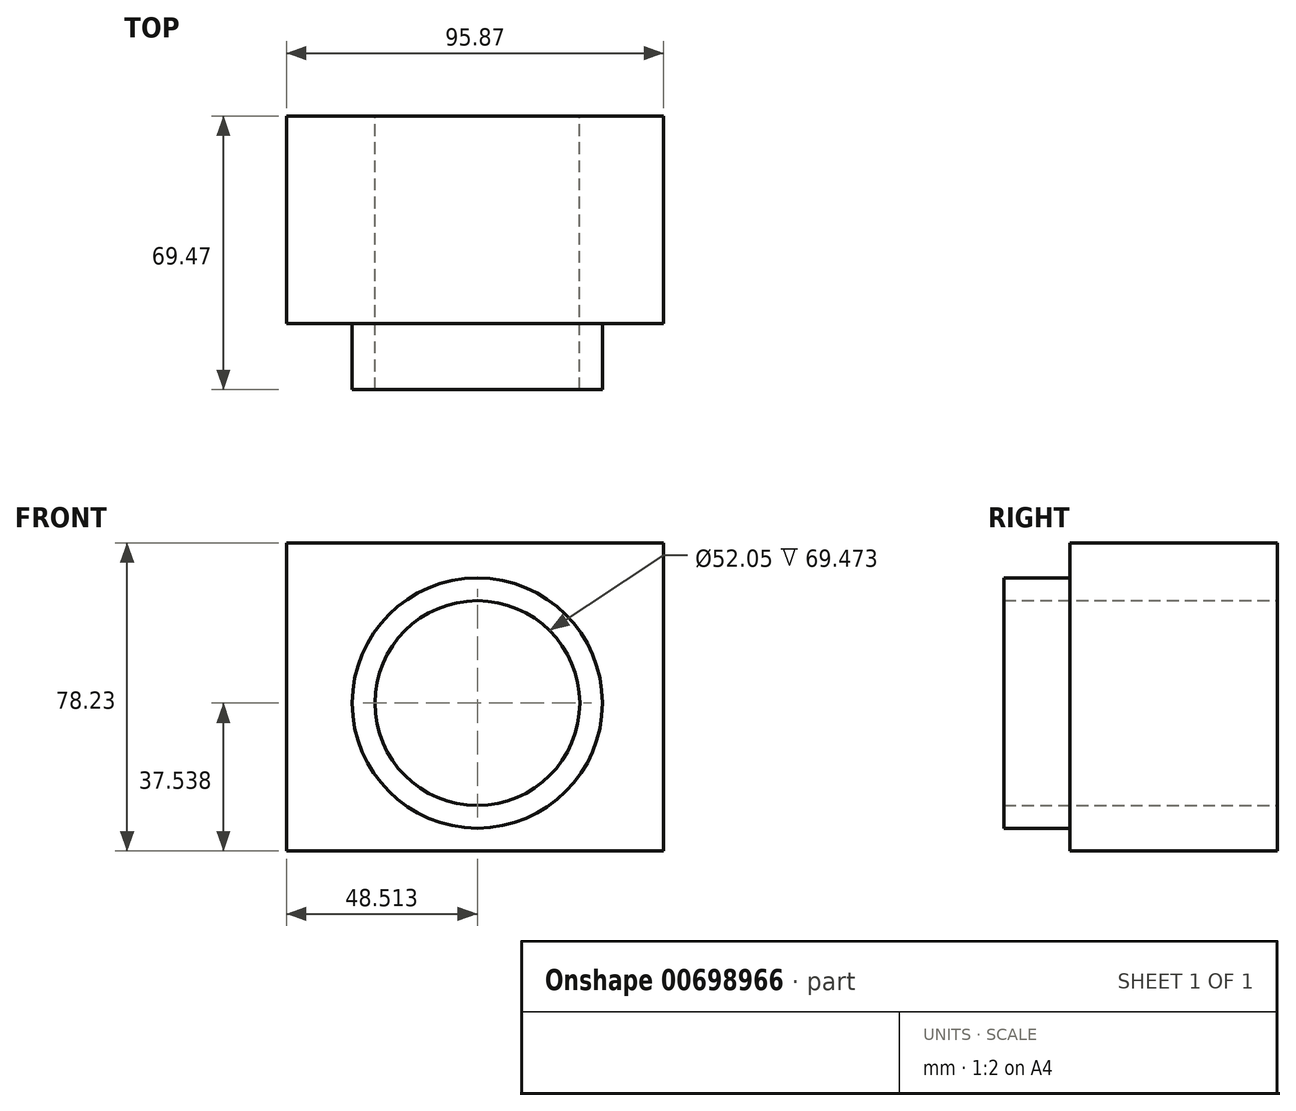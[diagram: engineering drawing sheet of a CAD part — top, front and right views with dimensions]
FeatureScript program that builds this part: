
annotation { "Feature Type Name" : "Feature", "Feature Type Description" : "" }
export const myFeature = defineFeature(function(context is Context, id is Id, definition is map)
    precondition{}
    {
        {
            var Q0;
            Q0=qCreatedBy(makeId("Top.planeOp"),FACE);
            var sketch = newSketch(context, id + "F0", { "sketchPlane" : qUnion([Q0])});
            skLineSegment(sketch, "E0.bottom", {"start": v(-36.09, -29.74) * mm, "end": v(59.78, -29.74) * mm});
            skLineSegment(sketch, "E0.top", {"start": v(-36.09, 22.97) * mm, "end": v(59.78, 22.97) * mm});
            skLineSegment(sketch, "E0.left", {"start": v(-36.09, -29.74) * mm, "end": v(-36.09, 22.97) * mm});
            skLineSegment(sketch, "E0.right", {"start": v(59.78, -29.74) * mm, "end": v(59.78, 22.97) * mm});
            skSolve(sketch);
        }
        {
            var Q0;
            Q0=makeQuery(id+"F0.imprint","IMPRINT",FACE,{"disambiguationData":[TD([[makeQuery(id+"F0.imprint","IMPRINT",EDGE,{"derivedFrom":sQuery(id+"F0.wireOp",EDGE,"E0.bottom")}),1.0]])]});
            extrude(context, id + "F1", {"entities" : qUnion([Q0]), "depth" : 78.23 * mm, "offsetDistance" : 25.4 * mm});
        }
        {
            var Q0;
            Q0=makeQuery(id+"F1.opExtrude","SWEPT_FACE",FACE,{"disambiguationData":[OSD([sQuery(id+"F0.wireOp",EDGE,"E0.bottom")])]});
            var sketch = newSketch(context, id + "F2", { "sketchPlane" : qUnion([Q0])});
            skCircle(sketch, "E1", {"center": v(12.42, 37.54) * mm, "radius": 31.77 * mm});
            skCircle(sketch, "E2", {"center": v(12.42, 37.54) * mm, "radius": 26.02 * mm});
            skSolve(sketch);
        }
        {
            var Q0;
            Q0=makeQuery(id+"F2.imprint","IMPRINT",FACE,{"disambiguationData":[TD([[makeQuery(id+"F2.imprint","IMPRINT",EDGE,{"derivedFrom":sQuery(id+"F2.wireOp",EDGE,"E1")}),1.0]])]});
            extrude(context, id + "F3", {"entities" : qUnion([Q0]), "operationType" : NewBodyOperationType.ADD, "depth" : 16.76 * mm, "offsetDistance" : 25.4 * mm});
        }
        {
            var Q0;
            Q0=makeQuery(id+"F3.boolean.opBoolean","SPLIT",FACE,{"disambiguationData":[TD([makeQuery(id+"F3.opExtrude","SWEPT_FACE",FACE,{"disambiguationData":[OSD([sQuery(id+"F2.wireOp",EDGE,"E2")])]})])],"derivedFrom":makeQuery(id+"F1.opExtrude","SWEPT_FACE",FACE,{"disambiguationData":[OSD([sQuery(id+"F0.wireOp",EDGE,"E0.bottom")])]})});
            extrude(context, id + "F4", {"entities" : qUnion([Q0]), "operationType" : NewBodyOperationType.REMOVE, "oppositeDirection" : true, "depth" : 137.67 * mm, "offsetDistance" : 25.4 * mm});
        }
    });
